# Revit family: Hager-FW-IP30-With_Door-With_notch-sistema-NoHosted-CH-it
name_source: partatom
category: Electrical Equipment
units: mm (PartAtom-declared; Revit-internal decimal feet)

## family parameters
Always vertical = Yes
Cut with Voids When Loaded = No
Panel Configuration = Two Columns, Circuits Across
Part Type = Panelboard
Room Calculation Point = No
Round Connector Dimension = Use Diameter
Shared = No
Work Plane-Based = Yes

## types (20) — shared parameters
Default Elevation = 1219 mm
EF000003 - Tipo di montaggio = EV000128 - parete forata
EF000007 - colore = EV000202 - bianco
EF000049 - profondità = 125 mm  [stored 0.410105 ft]
EF000116 - numero RAL = 9010
EF000218 - profondità di incasso = 112 mm  [stored 0.367454 ft]
EF000339 - tipo di copertura = EV004216 - porta
EF001062 - esecuzione EMC = No
EF001088 - possibilità di applicazione = Yes
EF001131 - profondità interna = 112 mm  [stored 0.367454 ft]
EF001134 - barra DIN = Yes
EF001596 - Attacco Lampada = EV000179 - acciaio
EF002950 - Numero moduli DIN = 12
EF004462 - tipo di chiusura = EV000154 - altri
EF005474 - grado di protezione (IP) = EV006410 - IP30
EF006244 - coperchio/porta trasparente = No
EF006306 - con serratura = No
EF009212 - esecuzione coperchio = EV009916 - con taglio
EF015776 - Morsettiera di terra = No
EF015777 - Morsettiera neutra = No
EF015941 - Segnale di passaggio porta = No
HG000002 - Con porta = Yes
HG000003 - Gamma = FW
HG000005 - Spessore = 3 mm  [stored 0.00984252 ft]
HG000006 - Ad incasso = Yes
HG000011 - File vuote nella parte basse = No
HG000017 - Distanza tra i poli = 18 mm  [stored 0.0590551 ft]
Manufacturer = Hager
Type Comments = FW

## per-type parameters (varying)
| type | EF000008 - Larghezza | EF000040 - Altezza | EF000118 - con piastra di montaggio | EF000266 - numero di file | EF000332 - Altezza della parte incassata | EF000846 - larghezza di montaggio | HG000001 - Numero di colonne | HG000004 - Codice produttore | HG000007 - Numero di colonne vuote | HG000008 - Numero di file vuote | HG000009 - Porta doppia a battente | HG000010 - Porte asimmetriche | Model |
| incassato IP30 L353 A1003 P125 12 Unità di divisione - FWU61S1 | 353 mm  [stored 1.15814 ft] | 1003 mm  [stored 3.29068 ft] | No | 6 | 952 mm  [stored 3.12336 ft] | 310 mm  [stored 1.01706 ft] | 1 | FWU61S1 | 0 | 0 | No | No | FWU61S1 |
| incassato IP30 L353 A1153 P125 12 Unità di divisione - FWU71S1 | 353 mm  [stored 1.15814 ft] | 1153 mm | No | 7 | 1102 mm  [stored 3.61549 ft] | 310 mm  [stored 1.01706 ft] | 1 | FWU71S1 | 0 | 0 | No | No | FWU71S1 |
| incassato IP30 L353 A553 P125 12 Unità di divisione - FWU31S1 | 353 mm  [stored 1.15814 ft] | 553 mm  [stored 1.8143 ft] | No | 3 | 502 mm  [stored 1.64698 ft] | 310 mm  [stored 1.01706 ft] | 1 | FWU31S1 | 0 | 0 | No | No | FWU31S1 |
| incassato IP30 L353 A703 P125 12 Unità di divisione - FWU41S1 | 353 mm  [stored 1.15814 ft] | 703 mm  [stored 2.30643 ft] | No | 4 | 652 mm  [stored 2.13911 ft] | 310 mm  [stored 1.01706 ft] | 1 | FWU41S1 | 0 | 0 | No | No | FWU41S1 |
| incassato IP30 L353 A853 P125 12 Unità di divisione - FWU51S1 | 353 mm  [stored 1.15814 ft] | 853 mm  [stored 2.79856 ft] | No | 5 | 802 mm  [stored 2.63123 ft] | 310 mm  [stored 1.01706 ft] | 1 | FWU51S1 | 0 | 0 | No | No | FWU51S1 |
| incassato IP30 L603 A1003 P125 12 Unità di divisione - FWU62K | 603 mm | 1003 mm  [stored 3.29068 ft] | Yes | 6 | 952 mm  [stored 3.12336 ft] | 560 mm  [stored 1.83727 ft] | 1 | FWU62K | 1 | 6 | No | No | FWU62K |
| incassato IP30 L603 A1003 P125 12 Unità di divisione - FWU62S1 | 603 mm | 1003 mm  [stored 3.29068 ft] | No | 12 | 952 mm  [stored 3.12336 ft] | 560 mm  [stored 1.83727 ft] | 2 | FWU62S1 | 0 | 0 | No | No | FWU62S1 |
| incassato IP30 L603 A1153 P125 12 Unità di divisione - FWU72S1 | 603 mm | 1153 mm | No | 14 | 1102 mm  [stored 3.61549 ft] | 560 mm  [stored 1.83727 ft] | 2 | FWU72S1 | 0 | 0 | No | No | FWU72S1 |
| incassato IP30 L603 A553 P125 12 Unità di divisione - FWU32S1 | 603 mm | 553 mm  [stored 1.8143 ft] | No | 6 | 502 mm  [stored 1.64698 ft] | 560 mm  [stored 1.83727 ft] | 2 | FWU32S1 | 0 | 0 | No | No | FWU32S1 |
| incassato IP30 L603 A703 P125 12 Unità di divisione - FWU42K | 603 mm | 703 mm  [stored 2.30643 ft] | Yes | 4 | 652 mm  [stored 2.13911 ft] | 560 mm  [stored 1.83727 ft] | 1 | FWU42K | 1 | 4 | No | No | FWU42K |
| incassato IP30 L603 A703 P125 12 Unità di divisione - FWU42S1 | 603 mm | 703 mm  [stored 2.30643 ft] | No | 8 | 652 mm  [stored 2.13911 ft] | 560 mm  [stored 1.83727 ft] | 2 | FWU42S1 | 0 | 0 | No | No | FWU42S1 |
| incassato IP30 L603 A853 P125 12 Unità di divisione - FWU52K | 603 mm | 853 mm  [stored 2.79856 ft] | Yes | 5 | 802 mm  [stored 2.63123 ft] | 560 mm  [stored 1.83727 ft] | 1 | FWU52K | 1 | 5 | No | No | FWU52K |
| incassato IP30 L603 A853 P125 12 Unità di divisione - FWU52S1 | 603 mm | 853 mm  [stored 2.79856 ft] | No | 10 | 802 mm  [stored 2.63123 ft] | 560 mm  [stored 1.83727 ft] | 2 | FWU52S1 | 0 | 0 | No | No | FWU52S1 |
| incassato IP30 L853 A1003 P125 12 Unità di divisione - FWU63S1 | 853 mm  [stored 2.79856 ft] | 1003 mm  [stored 3.29068 ft] | No | 18 | 952 mm  [stored 3.12336 ft] | 810 mm | 3 | FWU63S1 | 0 | 0 | Yes | Yes | FWU63S1 |
| incassato IP30 L853 A1153 P125 12 Unità di divisione - FWU73S1 | 853 mm  [stored 2.79856 ft] | 1153 mm | No | 21 | 1102 mm  [stored 3.61549 ft] | 810 mm | 3 | FWU73S1 | 0 | 0 | Yes | Yes | FWU73S1 |
| incassato IP30 L853 A553 P125 12 Unità di divisione - FWU33S1 | 853 mm  [stored 2.79856 ft] | 553 mm  [stored 1.8143 ft] | No | 9 | 502 mm  [stored 1.64698 ft] | 810 mm | 3 | FWU33S1 | 0 | 0 | Yes | Yes | FWU33S1 |
| incassato IP30 L853 A703 P125 12 Unità di divisione - FWU43K | 853 mm  [stored 2.79856 ft] | 703 mm  [stored 2.30643 ft] | Yes | 8 | 652 mm  [stored 2.13911 ft] | 810 mm | 2 | FWU43K | 1 | 4 | Yes | Yes | FWU43K |
| incassato IP30 L853 A703 P125 12 Unità di divisione - FWU43S1 | 853 mm  [stored 2.79856 ft] | 703 mm  [stored 2.30643 ft] | No | 12 | 652 mm  [stored 2.13911 ft] | 810 mm | 3 | FWU43S1 | 0 | 0 | Yes | Yes | FWU43S1 |
| incassato IP30 L853 A853 P125 12 Unità di divisione - FWU53K | 853 mm  [stored 2.79856 ft] | 853 mm  [stored 2.79856 ft] | Yes | 10 | 802 mm  [stored 2.63123 ft] | 810 mm | 2 | FWU53K | 1 | 5 | Yes | Yes | FWU53K |
| incassato IP30 L853 A853 P125 12 Unità di divisione - FWU53S1 | 853 mm  [stored 2.79856 ft] | 853 mm  [stored 2.79856 ft] | No | 15 | 802 mm  [stored 2.63123 ft] | 810 mm | 3 | FWU53S1 | 0 | 0 | Yes | Yes | FWU53S1 |

note: [stored X ft] marks values corroborated as IEEE doubles in the binary element streams (Revit-internal decimal feet)

## geometry (parser evidence)
native form markers: Sweep x13
no freeform markers — native parametric forms only
